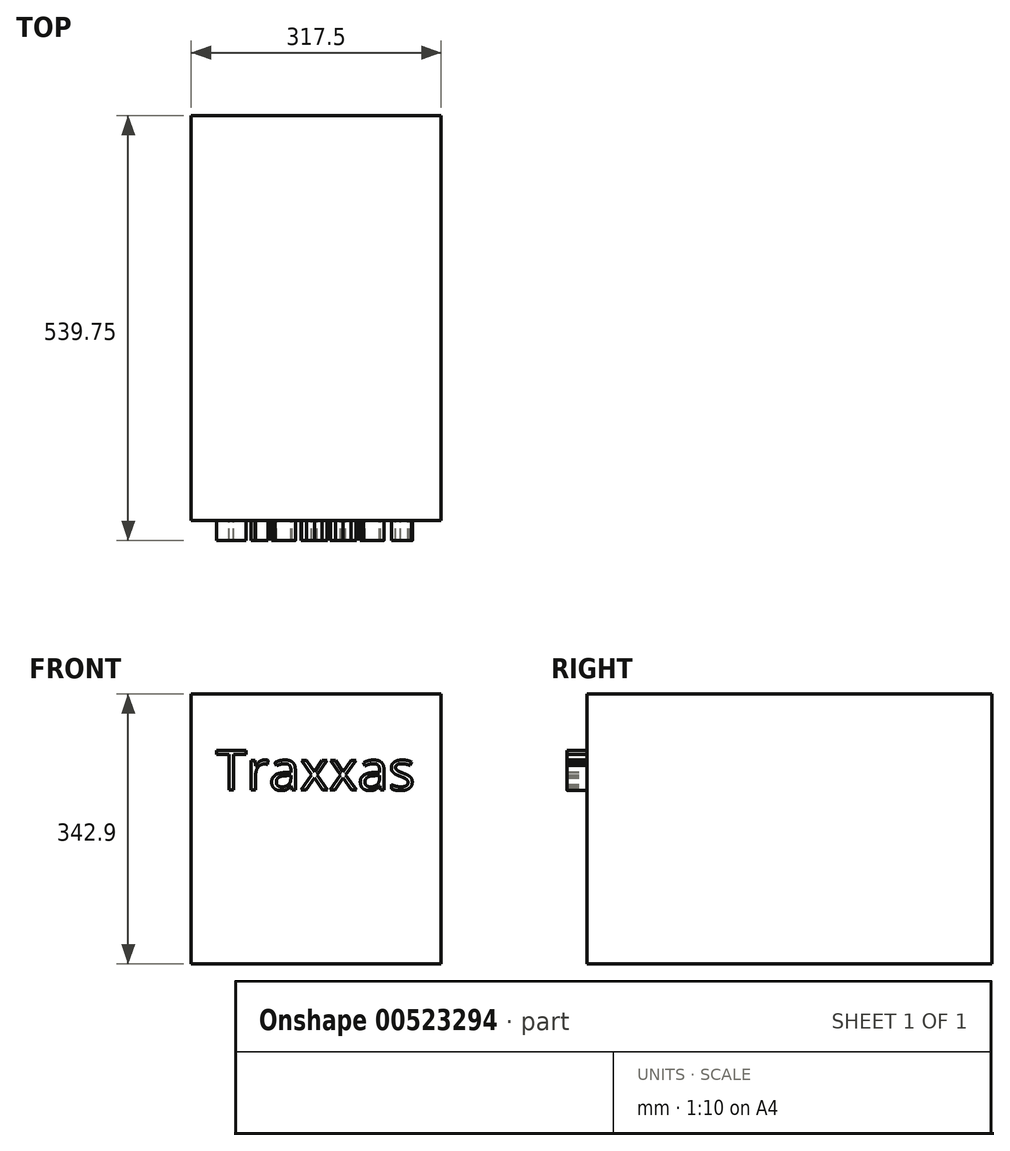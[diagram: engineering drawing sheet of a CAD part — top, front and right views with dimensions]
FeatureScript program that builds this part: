
annotation { "Feature Type Name" : "Feature", "Feature Type Description" : "" }
export const myFeature = defineFeature(function(context is Context, id is Id, definition is map)
    precondition{}
    {
        {
            var Q0;
            Q0=qCreatedBy(makeId("Front.planeOp"),FACE);
            var sketch = newSketch(context, id + "F0", { "sketchPlane" : qUnion([Q0])});
            skLineSegment(sketch, "E0.bottom", {"start": v(158.75, 171.45) * mm, "end": v(-158.75, 171.45) * mm});
            skLineSegment(sketch, "E0.top", {"start": v(158.75, -171.45) * mm, "end": v(-158.75, -171.45) * mm});
            skLineSegment(sketch, "E0.left", {"start": v(158.75, 171.45) * mm, "end": v(158.75, -171.45) * mm});
            skLineSegment(sketch, "E0.right", {"start": v(-158.75, 171.45) * mm, "end": v(-158.75, -171.45) * mm});
            skPoint(sketch, "E0.middle", {"position": v(0, 0) * mm});
            skSolve(sketch);
        }
        {
            var Q0;
            Q0=makeQuery(id+"F0.imprint","IMPRINT",FACE,{"disambiguationData":[TD([[makeQuery(id+"F0.imprint","IMPRINT",EDGE,{"derivedFrom":sQuery(id+"F0.wireOp",EDGE,"E0.bottom")}),1.0]])]});
            extrude(context, id + "F1", {"entities" : qUnion([Q0]), "depth" : 514.35 * mm, "offsetDistance" : 25.4 * mm});
        }
        {
            var Q0;
            Q0=makeQuery(id+"F1.opExtrude","CAP_FACE",FACE,{"disambiguationData":[OSD([sQuery(id+"F0.wireOp",EDGE,"E0.bottom"),sQuery(id+"F0.wireOp",EDGE,"E0.top"),sQuery(id+"F0.wireOp",EDGE,"E0.left"),sQuery(id+"F0.wireOp",EDGE,"E0.right")])],"isStart":false});
            var sketch = newSketch(context, id + "F2", { "sketchPlane" : qUnion([Q0])});
            skText(sketch, "E1", { "text": "Traxxas", "fontName": "OpenSans-Regular.ttf"});
            const initialGuessF2  = {"E1": [-0.12747, 0.0494, 1, 0, 0.05055]};
            skSetInitialGuess(sketch, initialGuessF2);
            skSolve(sketch);
        }
        {
            var Q0;
            Q0 = qSketchRegion(id + "F2", true);
            extrude(context, id + "F3", {"entities" : qUnion([Q0]), "operationType" : NewBodyOperationType.ADD, "depth" : 25.4 * mm, "offsetDistance" : 25.4 * mm});
        }
    });
